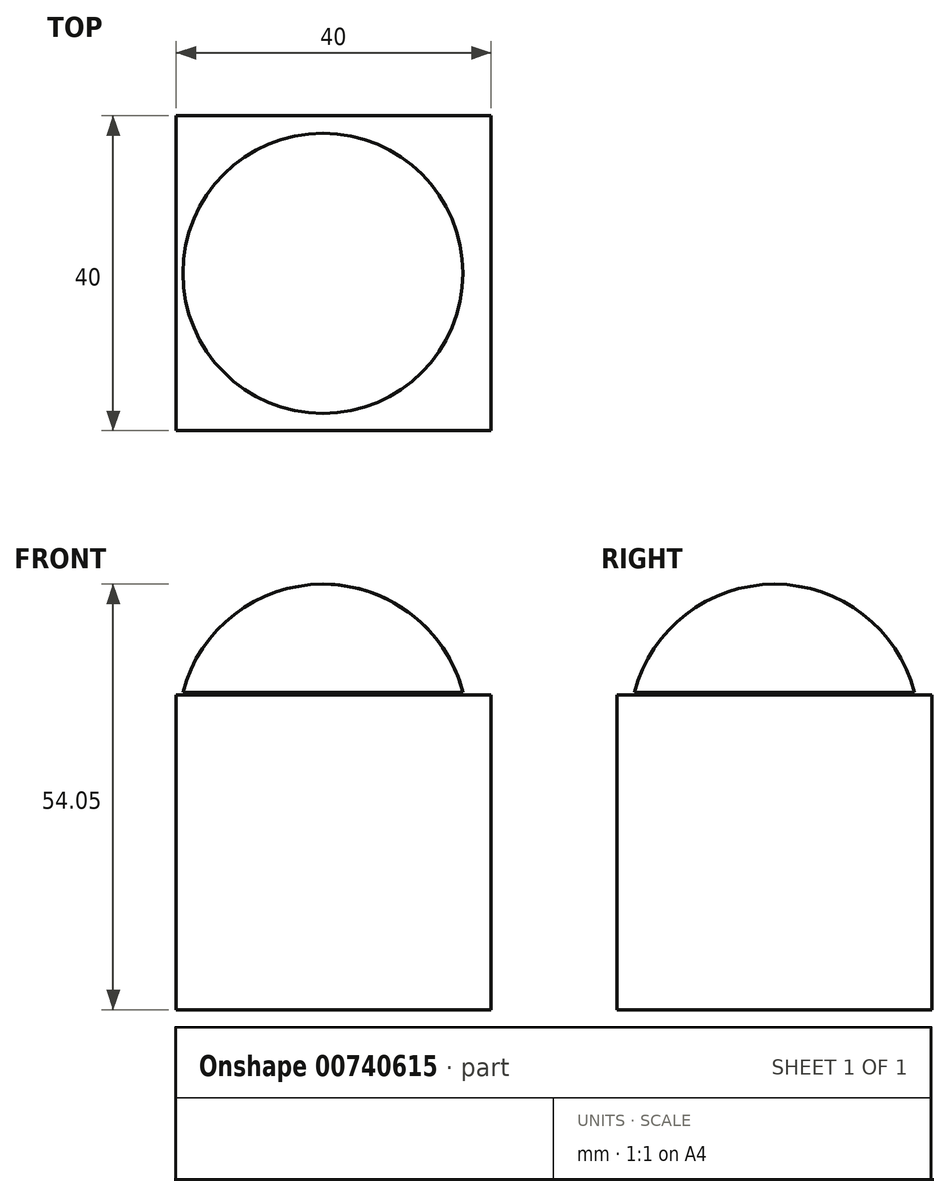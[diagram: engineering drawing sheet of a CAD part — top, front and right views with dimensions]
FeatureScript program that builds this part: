
annotation { "Feature Type Name" : "Feature", "Feature Type Description" : "" }
export const myFeature = defineFeature(function(context is Context, id is Id, definition is map)
    precondition{}
    {
        {
            var Q0;
            Q0=qCreatedBy(makeId("Top.planeOp"),FACE);
            var sketch = newSketch(context, id + "F0", { "sketchPlane" : qUnion([Q0])});
            skLineSegment(sketch, "E0.bottom", {"start": v(-18.63, 20) * mm, "end": v(21.37, 20) * mm});
            skLineSegment(sketch, "E0.top", {"start": v(-18.63, -20) * mm, "end": v(21.37, -20) * mm});
            skLineSegment(sketch, "E0.left", {"start": v(-18.63, 20) * mm, "end": v(-18.63, -20) * mm});
            skLineSegment(sketch, "E0.right", {"start": v(21.37, 20) * mm, "end": v(21.37, -20) * mm});
            skPoint(sketch, "E0.middle", {"position": v(1.37, 0) * mm});
            skSolve(sketch);
        }
        {
            var Q0;
            Q0 = qSketchRegion(id + "F0", true);
            extrude(context, id + "F1", {"entities" : qUnion([Q0]), "endBound" : BoundingType.SYMMETRIC, "depth" : 40 * mm, "offsetDistance" : 25 * mm});
        }
        {
            var Q0;
            Q0=qCreatedBy(makeId("Front.planeOp"),FACE);
            var sketch = newSketch(context, id + "F2", { "sketchPlane" : qUnion([Q0])});
            skLineSegment(sketch, "E1", {"start": v(0, -20.08) * mm, "end": v(0, 36.4) * mm});
            skSolve(sketch);
        }
        {
            var Q0;
            Q0=qCreatedBy(makeId("Front.planeOp"),FACE);
            var sketch = newSketch(context, id + "F3", { "sketchPlane" : qUnion([Q0])});
            skArc(sketch, "E2", {"start": v(17.8, 20.32) * mm, "mid": v(11.24, 30.22) * mm, "end": v(0, 34.05) * mm});
            skLineSegment(sketch, "E3", {"start": v(-17.8, 20.32) * mm, "end": v(17.8, 20.32) * mm});
            skLineSegment(sketch, "E4", {"start": v(0, 34.05) * mm, "end": v(0, 20.32) * mm});
            skSolve(sketch);
        }
        {
            var Q0;
            {var subQ0=sQuery(id+"F3.wireOp",EDGE,"E2");Q0=makeQuery(id+"F3.imprint","IMPRINT",FACE,{"disambiguationData":[TD([[makeQuery(id+"F3.imprint","IMPRINT",EDGE,{"derivedFrom":subQ0}),1.0]])]});}
            var Q1;
            Q1=sQuery(id+"F2.wireOp",EDGE,"E1");
            revolve(context, id + "F4", {"surfaceOperationType" : NewSurfaceOperationType.NEW, "entities" : qUnion([Q0]), "axis" : qUnion([Q1]), "revolveType" : RevolveType.FULL});
        }
    });
